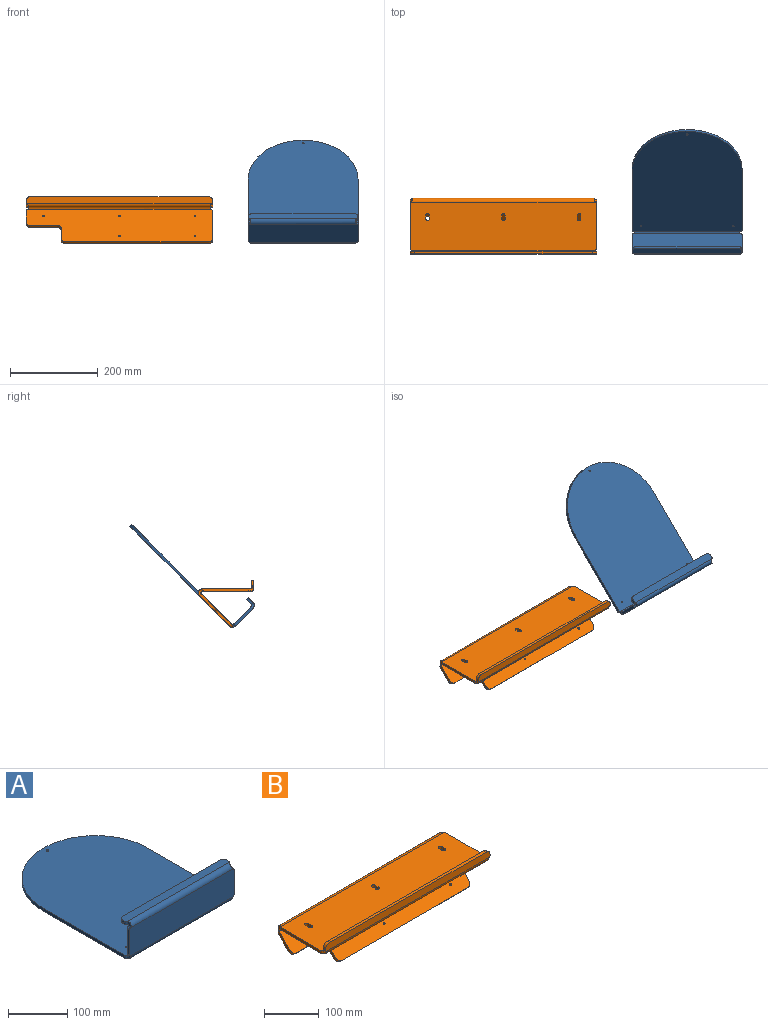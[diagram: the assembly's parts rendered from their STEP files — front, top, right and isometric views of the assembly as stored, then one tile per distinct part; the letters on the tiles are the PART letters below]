
ASSEMBLY  parts=2 mates=1
PART A: 35 faces, bbox 250x331x76 mm
  f0: plane 194x6mm, normal (-1,0,0), area 1164mm2, adj f1,f6,f7,f9
  f1: cylinder r=125mm len=250mm, axis (0,0,1), area 2356.2mm2, adj f0,f2,f6,f7
  f2: plane 194x6mm, normal (1,0,0), area 1164mm2, adj f1,f6,f7,f8
  f3: cylinder r=2.1mm len=6mm, axis (0,0,1), area 79.2mm2, adj f6,f7
  f4: cylinder r=2.1mm len=6mm, axis (0,0,1), area 79.2mm2, adj f6,f7
  f5: cylinder r=2.1mm len=6mm, axis (0,0,1), area 79.2mm2, adj f6,f7
  f6: plane 322x250mm, normal (0,0,-1), area 73748.3mm2, adj f0,f1,f2,f3,f4,f5,f8,f9
  f7: plane 322x250mm, normal (0,0,1), area 73748.3mm2, adj f0,f1,f2,f3,f4,f5,f8,f9
  f8: cylinder r=3mm len=6mm, axis (0,0,-1), area 28.3mm2, adj f2,f6,f7,f18
  f9: cylinder r=3mm len=6mm, axis (0,0,1), area 28.3mm2, adj f0,f6,f7,f19
  f10: plane 52x6mm, normal (-1,0,0), area 312mm2, adj f12,f13,f14,f17
  f11: plane 52x6mm, normal (1,0,0), area 312mm2, adj f12,f13,f15,f16
  f12: plane 250x58mm, normal (0,-1,0), area 14492.3mm2, adj f10,f11,f14,f15,f16,f17,f20,f33
  f13: plane 250x58mm, normal (0,1,0), area 14492.3mm2, adj f10,f11,f14,f15,f16,f17,f21,f34
  f14: cylinder r=3mm len=6mm, axis (0,1,0), area 28.3mm2, adj f10,f12,f13,f32
  f15: cylinder r=3mm len=6mm, axis (0,1,0), area 28.3mm2, adj f11,f12,f13,f31
  f16: cylinder r=3mm len=6mm, axis (0,1,0), area 28.3mm2, adj f11,f12,f13,f18
  f17: cylinder r=3mm len=6mm, axis (0,1,0), area 28.3mm2, adj f10,f12,f13,f19
  f18: bspline ~9x9mm, area 63.6mm2, adj f8,f16,f20,f21
  f19: bspline ~9x9mm, area 62.4mm2, adj f9,f17,f20,f21
  f20: cylinder r=9mm len=244mm, axis (-1,0,0), area 3412.4mm2, adj f6,f12,f18,f19
  f21: cylinder r=3mm len=244mm, axis (-1,0,0), area 1137.5mm2, adj f7,f13,f18,f19
  f22: plane 6x3mm, normal (1,0,0), area 18mm2, adj f25,f26,f27,f29
  f23: plane 230x6mm, normal (0,1,0), area 1380mm2, adj f25,f26,f29,f30
  f24: plane 6x3mm, normal (-1,0,0), area 18mm2, adj f25,f26,f28,f30
  f25: plane 250x16mm, normal (0,0,1), area 3953.2mm2, adj f22,f23,f24,f27,f28,f29,f30,f33
  f26: plane 250x16mm, normal (0,0,-1), area 3953.2mm2, adj f22,f23,f24,f27,f28,f29,f30,f34
  f27: cylinder r=3mm len=6mm, axis (0,0,-1), area 28.3mm2, adj f22,f25,f26,f31
  f28: cylinder r=3mm len=6mm, axis (0,0,-1), area 28.3mm2, adj f24,f25,f26,f32
  f29: cylinder r=10mm len=10mm, axis (0,0,1), area 94.2mm2, adj f22,f23,f25,f26
  f30: cylinder r=10mm len=10mm, axis (0,0,1), area 94.2mm2, adj f23,f24,f25,f26
  f31: bspline ~9x9mm, area 63.2mm2, adj f15,f27,f33,f34
  f32: bspline ~9x9mm, area 64.2mm2, adj f14,f28,f33,f34
  f33: cylinder r=9mm len=244mm, axis (1,0,0), area 3410mm2, adj f12,f25,f31,f32
  f34: cylinder r=3mm len=244mm, axis (1,0,0), area 1136.7mm2, adj f13,f26,f31,f32
PART B: 55 faces, bbox 425x127.3x107.4 mm
  f0: plane 103.27x6mm, normal (1,0,0), area 619.6mm2, adj f14,f15,f17,f19
  f1: plane 103.27x6mm, normal (-1,0,0), area 619.6mm2, adj f14,f15,f16,f18
  f2: plane 6.09x6mm, normal (1,0,0), area 36.1mm2, adj f3,f13,f14,f15
  f3: extruded ~8x6mm, area 91.6mm2, adj f2,f4,f14,f15
  f4: plane 6x5.95mm, normal (-1,0,0), area 35.3mm2, adj f3,f13,f14,f15
  f5: plane 6.09x6mm, normal (1,0,0), area 36.1mm2, adj f6,f12,f14,f15
  f6: extruded ~8x6mm, area 91.6mm2, adj f5,f7,f14,f15
  f7: plane 6x5.95mm, normal (-1,0,0), area 35.3mm2, adj f6,f12,f14,f15
  f8: plane 6.09x6mm, normal (1,0,0), area 36.1mm2, adj f9,f11,f14,f15
  f9: extruded ~8x6mm, area 91.6mm2, adj f8,f10,f14,f15
  f10: plane 6x5.95mm, normal (-1,0,0), area 35.3mm2, adj f9,f11,f14,f15
  f11: extruded ~8x6mm, area 92.4mm2, adj f8,f10,f14,f15
  f12: extruded ~8x6mm, area 92.4mm2, adj f5,f7,f14,f15
  f13: extruded ~8x6mm, area 92.4mm2, adj f2,f4,f14,f15
  f14: plane 425x109.27mm, normal (0,0,-1), area 46075.6mm2, adj f0,f1,f2,f3,f4,f5,f6,f7
  f15: plane 425x109.27mm, normal (0,0,1), area 46075.7mm2, adj f0,f1,f2,f3,f4,f5,f6,f7
  f16: cylinder r=3mm len=6mm, axis (0,0,1), area 28.3mm2, adj f1,f14,f15,f29
  f17: cylinder r=3mm len=6mm, axis (0,0,-1), area 28.3mm2, adj f0,f14,f15,f30
  f18: cylinder r=3mm len=6mm, axis (0,0,1), area 28.3mm2, adj f1,f14,f15,f52
  f19: cylinder r=3mm len=6mm, axis (0,0,-1), area 28.3mm2, adj f0,f14,f15,f51
  f20: plane 6x3mm, normal (1,0,0), area 18mm2, adj f23,f24,f26,f28
  f21: plane 405x6mm, normal (0,0,1), area 2430mm2, adj f23,f24,f26,f27
  f22: plane 6x3mm, normal (-1,0,0), area 18mm2, adj f23,f24,f25,f27
  f23: plane 425x16mm, normal (0,-1,0), area 6753.2mm2, adj f20,f21,f22,f25,f26,f27,f28,f31
  f24: plane 425x16mm, normal (0,1,0), area 6753.2mm2, adj f20,f21,f22,f25,f26,f27,f28,f32
  f25: cylinder r=3mm len=6mm, axis (0,1,0), area 28.3mm2, adj f22,f23,f24,f29
  f26: cylinder r=10mm len=10mm, axis (0,-1,0), area 94.2mm2, adj f20,f21,f23,f24
  f27: cylinder r=10mm len=10mm, axis (0,-1,0), area 94.2mm2, adj f21,f22,f23,f24
  f28: cylinder r=3mm len=6mm, axis (0,1,0), area 28.3mm2, adj f20,f23,f24,f30
  f29: bspline ~9x9mm, area 64.2mm2, adj f16,f25,f31,f32
  f30: bspline ~9x9mm, area 63.1mm2, adj f17,f28,f31,f32
  f31: cylinder r=9mm len=419mm, axis (1,0,0), area 5884.3mm2, adj f14,f23,f29,f30
  f32: cylinder r=3mm len=419mm, axis (1,0,0), area 1961.4mm2, adj f15,f24,f29,f30
  f33: plane 325x4.24mm, normal (0,-0.71,-0.71), area 1950mm2, adj f43,f44,f46,f49
  f34: plane 68.07x68.07mm, normal (1,0,0), area 541.6mm2, adj f43,f44,f46,f47
  f35: plane 30.41x30.41mm, normal (-1,0,0), area 222mm2, adj f43,f44,f45,f48
  f36: plane 60x4.24mm, normal (0,-0.71,-0.71), area 360mm2, adj f43,f44,f48,f50
  f37: plane 27.77x27.77mm, normal (-1,0,0), area 199.6mm2, adj f43,f44,f49,f50
  f38: cylinder r=2.1mm len=7.21mm, axis (0,-0.71,0.71), area 79.2mm2, adj f43,f44
  f39: cylinder r=2.1mm len=7.21mm, axis (0,-0.71,0.71), area 79.2mm2, adj f43,f44
  f40: cylinder r=2.1mm len=7.21mm, axis (0,-0.71,0.71), area 79.2mm2, adj f43,f44
  f41: cylinder r=2.1mm len=7.21mm, axis (0,-0.71,0.71), area 79.2mm2, adj f43,f44
  f42: cylinder r=2.1mm len=7.21mm, axis (0,-0.71,0.71), area 79.2mm2, adj f43,f44
  f43: plane 425x73.02mm, normal (0,-0.71,0.71), area 39512.8mm2, adj f33,f34,f35,f36,f37,f38,f39,f40
  f44: plane 425x73.02mm, normal (0,0.71,-0.71), area 39512.8mm2, adj f33,f34,f35,f36,f37,f38,f39,f40
  f45: cylinder r=3mm len=6.36mm, axis (0,0.71,-0.71), area 28.3mm2, adj f35,f43,f44,f52
  f46: cylinder r=10mm len=11.31mm, axis (0,-0.71,0.71), area 94.2mm2, adj f33,f34,f43,f44
  f47: cylinder r=3mm len=6.36mm, axis (0,0.71,-0.71), area 28.3mm2, adj f34,f43,f44,f51
  f48: cylinder r=10mm len=11.31mm, axis (0,-0.71,0.71), area 94.2mm2, adj f35,f36,f43,f44
  f49: cylinder r=10mm len=11.31mm, axis (0,0.71,-0.71), area 94.2mm2, adj f33,f37,f43,f44
  f50: cylinder r=10mm len=11.31mm, axis (0,-0.71,0.71), area 94.2mm2, adj f36,f37,f43,f44
  f51: bspline ~15.36x9.01mm, area 91.1mm2, adj f19,f47,f53,f54
  f52: bspline ~15.36x9mm, area 90.5mm2, adj f18,f45,f53,f54
  f53: cylinder r=3mm len=419mm, axis (1,0,0), area 2940.4mm2, adj f14,f43,f51,f52
  f54: cylinder r=9mm len=419mm, axis (1,0,0), area 8821.1mm2, adj f15,f44,f51,f52
PLACE A rot(axis=(1,0,0),45deg) t=(623.94,-58.49,101.02)mm
PLACE B t=(-394.31,-99.49,138.57)mm
MATE fastened A.f6 <-> B.f44  axis (0,0.71,-0.71) through (130.34,5,167.34)mm
